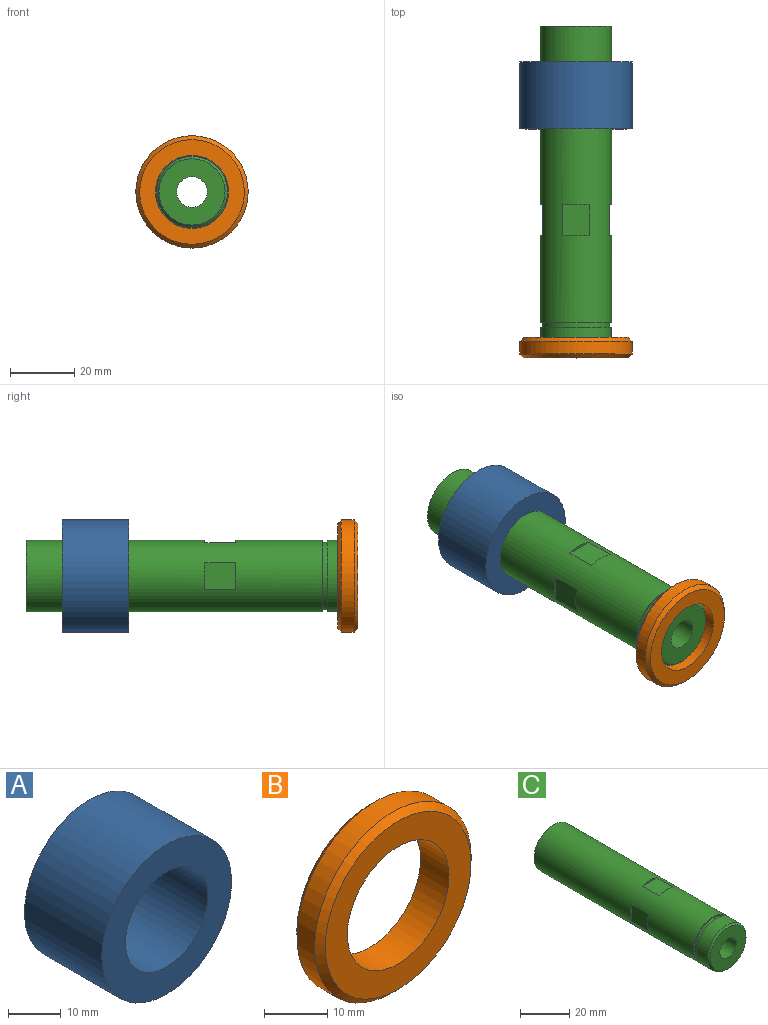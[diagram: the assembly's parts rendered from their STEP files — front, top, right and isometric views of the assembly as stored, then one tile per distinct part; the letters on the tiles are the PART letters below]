
ASSEMBLY  parts=3 mates=2
PART A: 4 faces, bbox 34.9x20.8x34.9 mm
  f0: cylinder r=11.11mm len=22.23mm, axis (0,1,0), area 1454.3mm2, adj f2,f3
  f1: cylinder r=17.46mm len=34.93mm, axis (0,1,0), area 2285.3mm2, adj f2,f3
  f2: plane 34.93x34.93mm, normal (0,-1,0), area 570mm2, adj f0,f1
  f3: plane 34.93x34.93mm, normal (0,1,0), area 570mm2, adj f0,f1
PART B: 6 faces, bbox 34.9x6.4x34.9 mm
  f0: cylinder r=11.35mm len=22.71mm, axis (0,1,0), area 453mm2, adj f2,f3
  f1: cylinder r=17.46mm len=34.93mm, axis (0,1,0), area 434.8mm2, adj f4,f5
  f2: plane 32.54x32.54mm, normal (0,-1,0), area 426.5mm2, adj f0,f4
  f3: plane 32.54x32.54mm, normal (0,1,0), area 426.5mm2, adj f0,f5
  f4: cone r=16.27mm half-angle=45deg, axis (0,1,0), area 178.9mm2, adj f1,f2
  f5: cone r=17.46mm half-angle=45deg, axis (0,-1,0), area 178.9mm2, adj f1,f3
PART C: 19 faces, bbox 22.2x100.8x22.2 mm
  f0: plane 20.57x20.57mm, normal (0,-1,0), area 261.2mm2, adj f1,f9
  f1: cylinder r=4.76mm len=49.89mm, axis (0,-1,0), area 1492.9mm2, adj f0,f2
  f2: cone r=4.76mm half-angle=1.4deg, axis (0,1,0), area 1727.4mm2, adj f1,f3
  f3: plane 22.23x22.23mm, normal (0,1,0), area 273.6mm2, adj f2,f4
  f4: cylinder r=11.11mm len=92.09mm, axis (0,-1,0), area 6188.1mm2, adj f3,f5,f10,f11,f12,f13,f14,f15
  f5: plane 22.23x22.23mm, normal (0,-1,0), area 38.9mm2, adj f4,f6
  f6: cylinder r=10.54mm len=21.08mm, axis (0,-1,0), area 105.1mm2, adj f5,f7
  f7: plane 22.1x22.1mm, normal (0,1,0), area 34.5mm2, adj f6,f8
  f8: cylinder r=11.05mm len=22.1mm, axis (0,-1,0), area 442.6mm2, adj f7,f9
  f9: cone r=10.29mm half-angle=45deg, axis (0,1,0), area 72.2mm2, adj f0,f8
  f10: plane 8.26x0.8mm, normal (0,1,0), area 4.4mm2, adj f4,f11
  f11: plane 9.53x8.26mm, normal (0,0,1), area 78.6mm2, adj f4,f10,f12
  f12: plane 8.26x0.8mm, normal (0,-1,0), area 4.4mm2, adj f4,f11
  f13: plane 9.53x8.26mm, normal (1,0,0), area 78.6mm2, adj f4,f14,f15
  f14: plane 8.26x0.8mm, normal (0,1,0), area 4.4mm2, adj f4,f13
  f15: plane 8.26x0.8mm, normal (0,-1,0), area 4.4mm2, adj f4,f13
  f16: plane 8.26x0.8mm, normal (0,1,0), area 4.4mm2, adj f4,f17
  f17: plane 9.53x8.26mm, normal (-1,0,0), area 78.6mm2, adj f4,f16,f18
  f18: plane 8.26x0.8mm, normal (0,-1,0), area 4.4mm2, adj f4,f17
PLACE A t=(6.46,54.51,17.33)mm
PLACE B t=(6.46,-31.17,17.33)mm
PLACE C t=(6.46,-22.48,17.33)mm
MATE fastened A.f0 <-> C.f1  axis (0,1,0) through (6.46,54.51,17.33)mm
MATE fastened B.f0 <-> C.f1  axis (0,1,0) through (6.46,-31.17,17.33)mm
